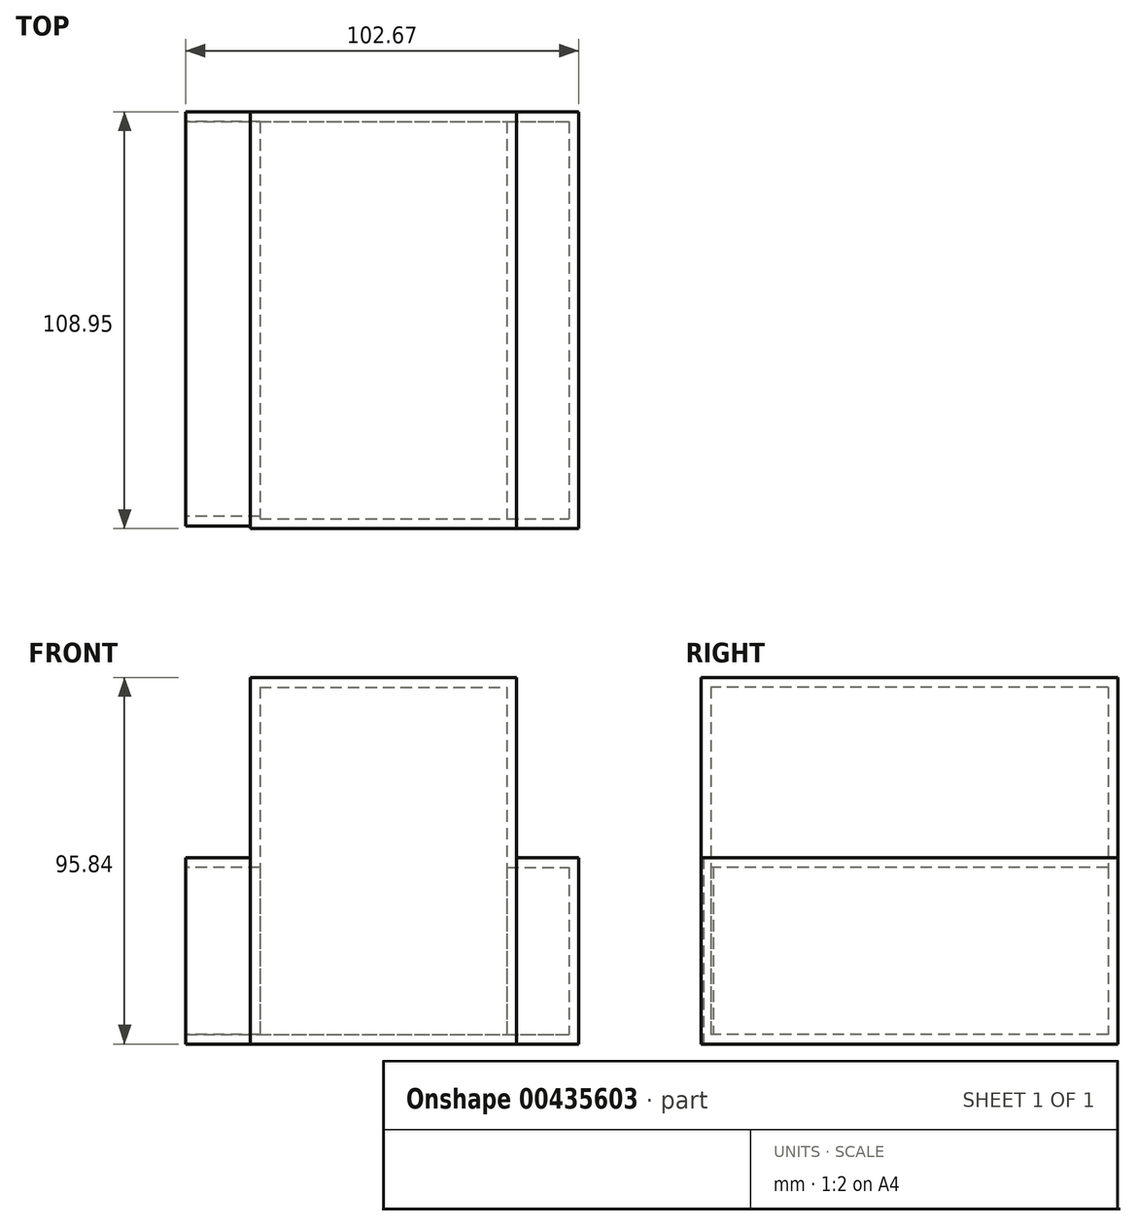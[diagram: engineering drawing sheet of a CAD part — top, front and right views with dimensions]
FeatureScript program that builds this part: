
annotation { "Feature Type Name" : "Feature", "Feature Type Description" : "" }
export const myFeature = defineFeature(function(context is Context, id is Id, definition is map)
    precondition{}
    {
        {
            var Q0;
            Q0=qCreatedBy(makeId("Top.planeOp"),FACE);
            var sketch = newSketch(context, id + "F0", { "sketchPlane" : qUnion([Q0])});
            skLineSegment(sketch, "E0.bottom", {"start": v(-31.93, 57.34) * mm, "end": v(37.77, 57.34) * mm});
            skLineSegment(sketch, "E0.top", {"start": v(-31.93, -51.61) * mm, "end": v(37.77, -51.61) * mm});
            skLineSegment(sketch, "E0.left", {"start": v(-31.93, 57.34) * mm, "end": v(-31.93, -51.61) * mm});
            skLineSegment(sketch, "E0.right", {"start": v(37.77, 57.34) * mm, "end": v(37.77, -51.61) * mm});
            skLineSegment(sketch, "E1.bottom", {"start": v(37.77, 57.34) * mm, "end": v(53.94, 57.34) * mm});
            skLineSegment(sketch, "E1.top", {"start": v(37.77, -51.57) * mm, "end": v(53.94, -51.57) * mm});
            skLineSegment(sketch, "E1.left", {"start": v(37.77, 57.34) * mm, "end": v(37.77, -51.57) * mm});
            skLineSegment(sketch, "E1.right", {"start": v(53.94, 57.34) * mm, "end": v(53.94, -51.57) * mm});
            skLineSegment(sketch, "E2.bottom", {"start": v(-31.93, 57.34) * mm, "end": v(-48.73, 57.34) * mm});
            skLineSegment(sketch, "E2.top", {"start": v(-31.93, -50.96) * mm, "end": v(-48.73, -50.96) * mm});
            skLineSegment(sketch, "E2.left", {"start": v(-31.93, 57.34) * mm, "end": v(-31.93, -50.96) * mm});
            skLineSegment(sketch, "E2.right", {"start": v(-48.73, 57.34) * mm, "end": v(-48.73, -50.96) * mm});
            skLineSegment(sketch, "E3.bottom", {"start": v(-48.73, 57.34) * mm, "end": v(-98.56, 57.34) * mm});
            skLineSegment(sketch, "E3.top", {"start": v(-48.73, -12.88) * mm, "end": v(-98.56, -12.88) * mm});
            skLineSegment(sketch, "E3.left", {"start": v(-48.73, 57.34) * mm, "end": v(-48.73, -12.88) * mm});
            skLineSegment(sketch, "E3.right", {"start": v(-98.56, 57.34) * mm, "end": v(-98.56, -12.88) * mm});
            skSolve(sketch);
        }
        {
            var Q0;
            Q0=makeQuery(id+"F0.imprint","IMPRINT",FACE,{"disambiguationData":[TD([[makeQuery(id+"F0.imprint","IMPRINT",EDGE,{"derivedFrom":sQuery(id+"F0.wireOp",EDGE,"E0.bottom")}),-1.0]])]});
            extrude(context, id + "F1", {"entities" : qUnion([Q0]), "depth" : 95.84 * mm});
        }
        {
            var Q0;
            Q0=makeQuery(id+"F0.imprint","IMPRINT",FACE,{"disambiguationData":[TD([[makeQuery(id+"F0.imprint","IMPRINT",EDGE,{"derivedFrom":sQuery(id+"F0.wireOp",EDGE,"E2.bottom")}),1.0]])]});
            var Q1;
            Q1=makeQuery(id+"F0.imprint","IMPRINT",FACE,{"disambiguationData":[TD([[makeQuery(id+"F0.imprint","IMPRINT",EDGE,{"derivedFrom":sQuery(id+"F0.wireOp",EDGE,"E1.bottom")}),-1.0]])]});
            extrude(context, id + "F2", {"entities" : qUnion([Q0, Q1]), "operationType" : NewBodyOperationType.ADD, "depth" : 48.78 * mm});
        }
        {
            var Q0;
            Q0=makeQuery(id+"F2.opExtrude","SWEPT_FACE",FACE,{"disambiguationData":[OSD([sQuery(id+"F0.wireOp",EDGE,"E2.right"),sQuery(id+"F0.wireOp",EDGE,"E3.left")])]});
            shell(context, id + "F3", {"entities" : qUnion([Q0]), "thickness" : 2.54 * mm});
        }
    });
